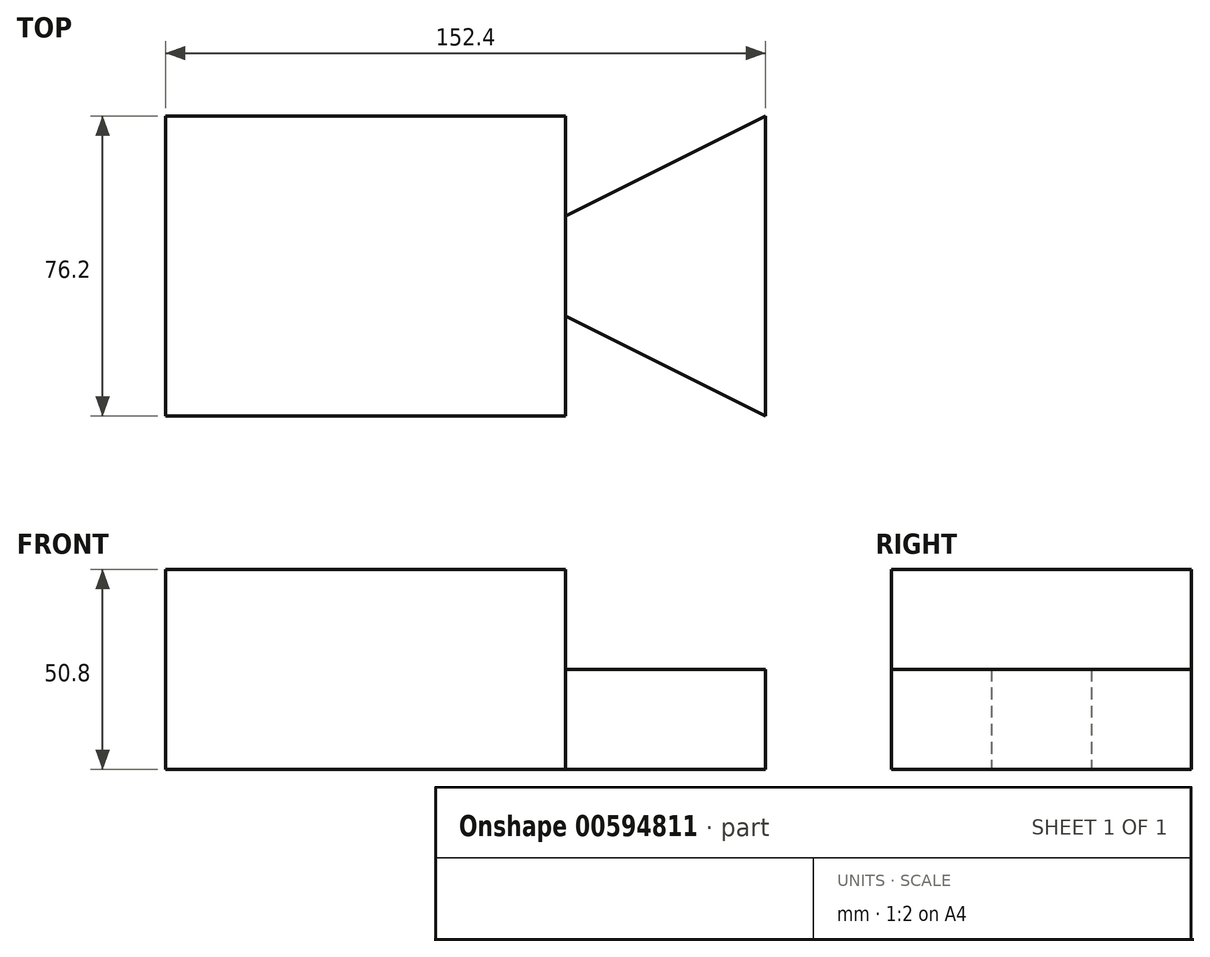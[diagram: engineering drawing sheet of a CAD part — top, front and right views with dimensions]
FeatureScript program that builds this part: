
annotation { "Feature Type Name" : "Feature", "Feature Type Description" : "" }
export const myFeature = defineFeature(function(context is Context, id is Id, definition is map)
    precondition{}
    {
        {
            var Q0;
            Q0=qCreatedBy(makeId("Top.planeOp"),FACE);
            var sketch = newSketch(context, id + "F0", { "sketchPlane" : qUnion([Q0])});
            skLineSegment(sketch, "E0.bottom", {"start": v(-83.5, 52.34) * mm, "end": v(18.1, 52.34) * mm});
            skLineSegment(sketch, "E0.top", {"start": v(-83.5, -23.86) * mm, "end": v(18.1, -23.86) * mm});
            skLineSegment(sketch, "E0.left", {"start": v(-83.5, 52.34) * mm, "end": v(-83.5, -23.86) * mm});
            skLineSegment(sketch, "E0.right", {"start": v(18.1, 52.34) * mm, "end": v(18.1, -23.86) * mm});
            skLineSegment(sketch, "E1", {"start": v(68.9, -23.86) * mm, "end": v(18.1, 1.54) * mm});
            skLineSegment(sketch, "E2", {"start": v(68.9, 52.34) * mm, "end": v(68.9, -23.86) * mm});
            skLineSegment(sketch, "E3", {"start": v(68.9, 52.34) * mm, "end": v(18.1, 26.94) * mm});
            skSolve(sketch);
        }
        {
            var Q0;
            {var subQ1=sQuery(id+"F0.wireOp",EDGE,"E0.bottom");Q0=makeQuery(id+"F0.imprint","IMPRINT",FACE,{"disambiguationData":[TD([[makeQuery(id+"F0.imprint","IMPRINT",EDGE,{"derivedFrom":subQ1}),-1.0]])]});}
            extrude(context, id + "F1", {"entities" : qUnion([Q0]), "depth" : 50.8 * mm, "offsetDistance" : 25.4 * mm});
        }
        {
            var Q0;
            {var subQ0=sQuery(id+"F0.wireOp",EDGE,"E1");Q0=makeQuery(id+"F0.imprint","IMPRINT",FACE,{"disambiguationData":[TD([[makeQuery(id+"F0.imprint","IMPRINT",EDGE,{"derivedFrom":subQ0}),-1.0]])]});}
            extrude(context, id + "F2", {"entities" : qUnion([Q0]), "operationType" : NewBodyOperationType.ADD, "depth" : 25.4 * mm, "offsetDistance" : 25.4 * mm});
        }
    });
